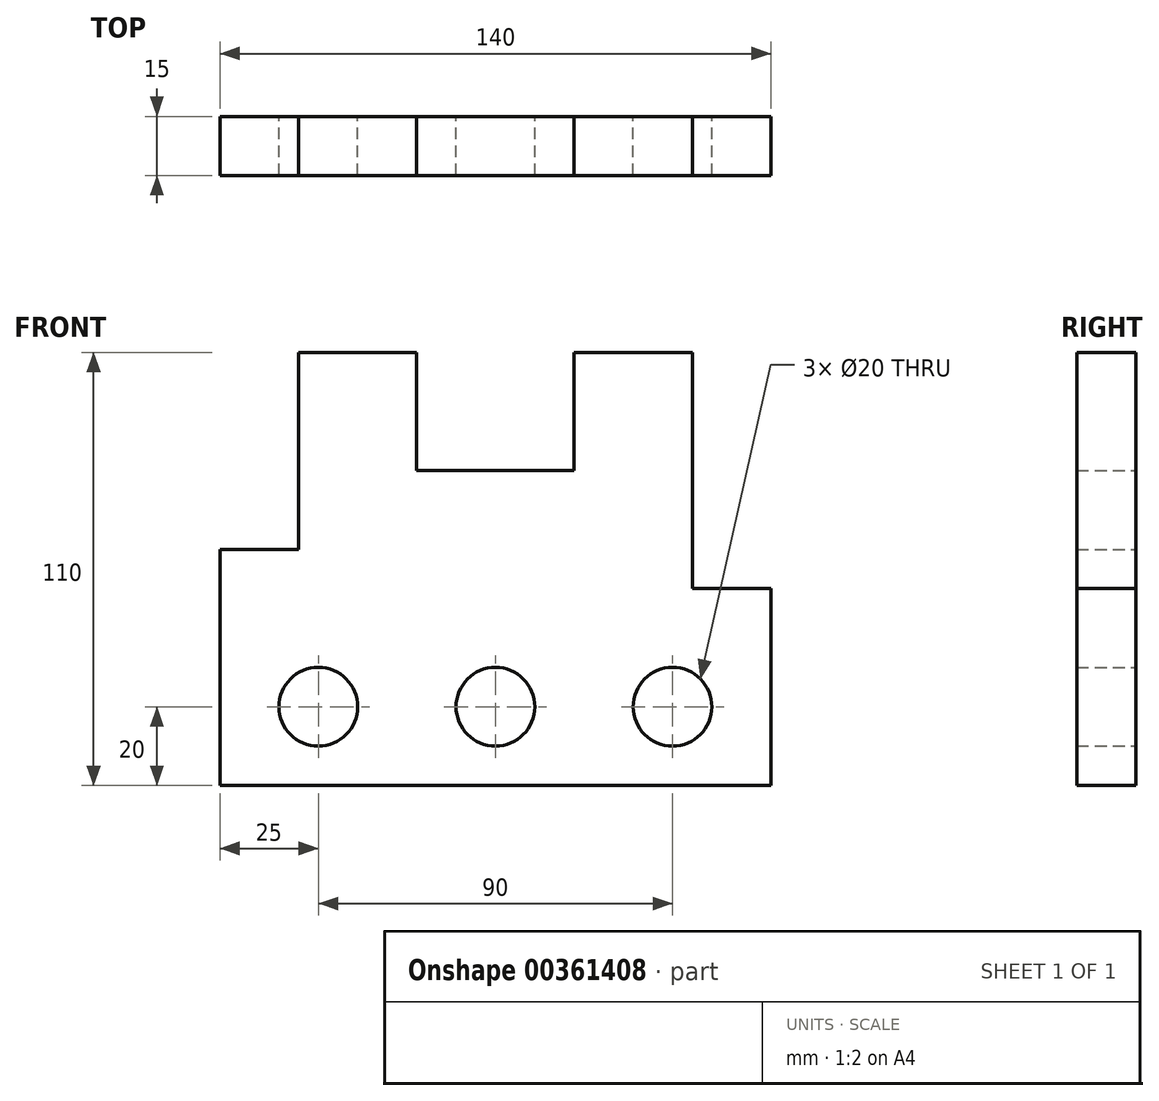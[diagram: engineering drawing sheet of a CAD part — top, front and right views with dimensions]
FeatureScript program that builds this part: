
annotation { "Feature Type Name" : "Feature", "Feature Type Description" : "" }
export const myFeature = defineFeature(function(context is Context, id is Id, definition is map)
    precondition{}
    {
        {
            var Q0;
            Q0=qCreatedBy(makeId("Front.planeOp"),FACE);
            var sketch = newSketch(context, id + "F0", { "sketchPlane" : qUnion([Q0])});
            skLineSegment(sketch, "E0", {"start": v(-140, 0) * mm, "end": v(-140, 60) * mm});
            skLineSegment(sketch, "E1", {"start": v(-140, 60) * mm, "end": v(-120, 60) * mm});
            skLineSegment(sketch, "E2", {"start": v(-120, 60) * mm, "end": v(-120, 110) * mm});
            skLineSegment(sketch, "E3", {"start": v(-120, 110) * mm, "end": v(-90, 110) * mm});
            skLineSegment(sketch, "E4", {"start": v(-90, 110) * mm, "end": v(-90, 80) * mm});
            skLineSegment(sketch, "E5", {"start": v(-90, 80) * mm, "end": v(-50, 80) * mm});
            skLineSegment(sketch, "E6", {"start": v(-50, 80) * mm, "end": v(-50, 110) * mm});
            skLineSegment(sketch, "E7", {"start": v(-50, 110) * mm, "end": v(-20, 110) * mm});
            skLineSegment(sketch, "E8", {"start": v(-20, 110) * mm, "end": v(-20, 50) * mm});
            skLineSegment(sketch, "E9", {"start": v(-20, 50) * mm, "end": v(0, 50) * mm});
            skLineSegment(sketch, "E10", {"start": v(0, 50) * mm, "end": v(0, 0) * mm});
            skLineSegment(sketch, "E11", {"start": v(0, 0) * mm, "end": v(-140, 0) * mm});
            skLineSegment(sketch, "E12", {"start": v(-140, 0) * mm, "end": v(-140, 0) * mm});
            skCircle(sketch, "E13", {"center": v(-115, 20) * mm, "radius": 10 * mm});
            skCircle(sketch, "E14", {"center": v(-70, 20) * mm, "radius": 10 * mm});
            skCircle(sketch, "E15", {"center": v(-25, 20) * mm, "radius": 10 * mm});
            skSolve(sketch);
        }
        {
            var Q0;
            Q0=makeQuery(id+"F0.imprint","IMPRINT",FACE,{"disambiguationData":[TD([[makeQuery(id+"F0.imprint","IMPRINT",EDGE,{"derivedFrom":sQuery(id+"F0.wireOp",EDGE,"E0")}),-1.0]])]});
            extrude(context, id + "F1", {"entities" : qUnion([Q0]), "depth" : 15 * mm});
        }
    });
